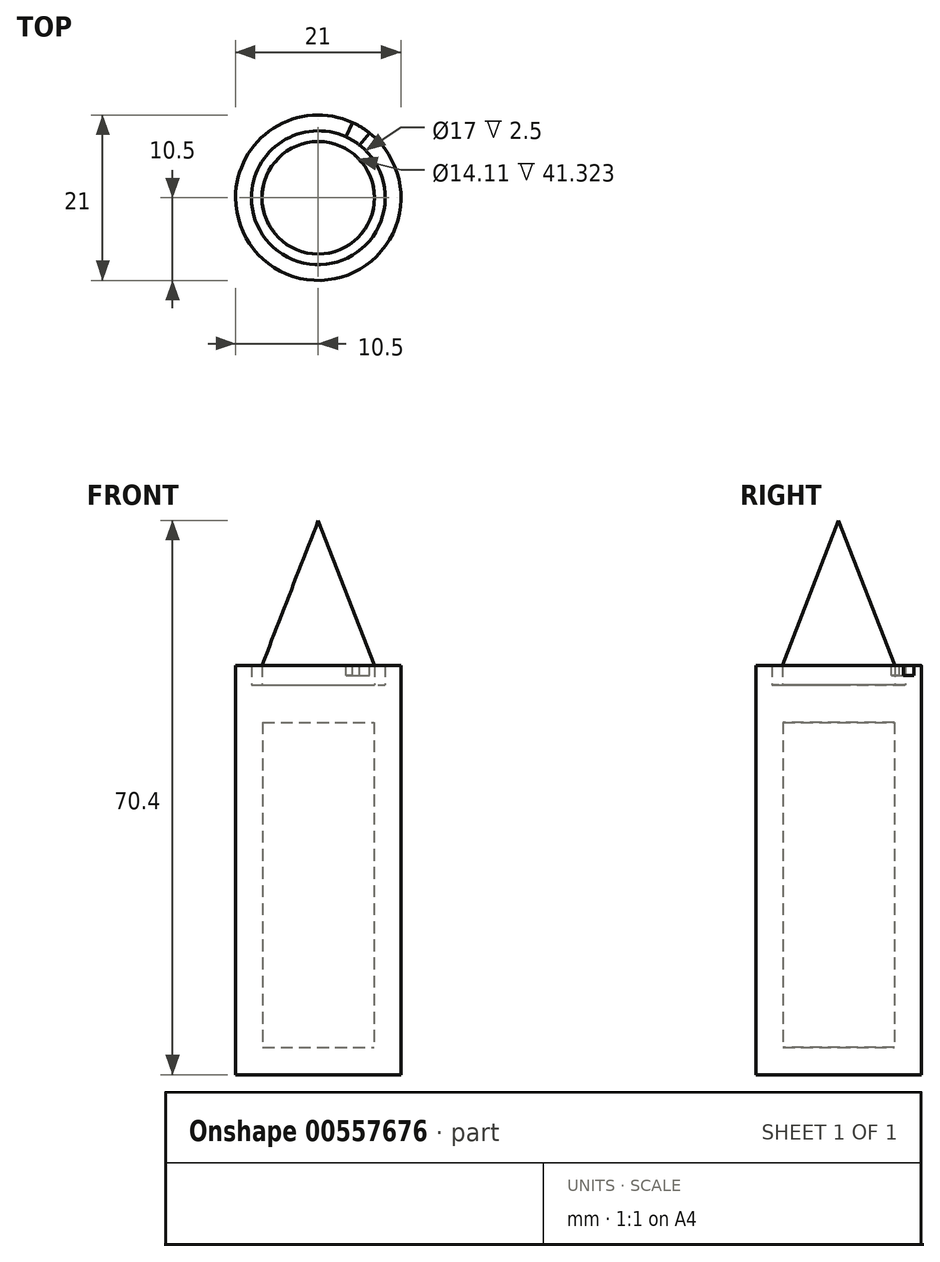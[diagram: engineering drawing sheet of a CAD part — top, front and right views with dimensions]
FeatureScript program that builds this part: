
annotation { "Feature Type Name" : "Feature", "Feature Type Description" : "" }
export const myFeature = defineFeature(function(context is Context, id is Id, definition is map)
    precondition{}
    {
        {
            var Q0;
            Q0=qCreatedBy(makeId("Front.planeOp"),FACE);
            var sketch = newSketch(context, id + "F0", { "sketchPlane" : qUnion([Q0])});
            skLineSegment(sketch, "E0", {"start": v(0, 0) * mm, "end": v(10.5, 0) * mm});
            skLineSegment(sketch, "E1", {"start": v(10.5, 0) * mm, "end": v(10.5, 52) * mm});
            skLineSegment(sketch, "E2", {"start": v(10.5, 52) * mm, "end": v(8.5, 52) * mm});
            skLineSegment(sketch, "E3", {"start": v(8.5, 52) * mm, "end": v(8.5, 49.5) * mm});
            skLineSegment(sketch, "E4", {"start": v(8.5, 49.5) * mm, "end": v(7.15, 49.5) * mm});
            skLineSegment(sketch, "E5", {"start": v(7.15, 49.5) * mm, "end": v(7.15, 52) * mm});
            skLineSegment(sketch, "E6", {"start": v(0, 0) * mm, "end": v(0, 70.4) * mm});
            skLineSegment(sketch, "E7", {"start": v(0, 70.4) * mm, "end": v(7.15, 52) * mm});
            skLineSegment(sketch, "E8.bottom", {"start": v(7.05, 3.45) * mm, "end": v(0, 3.45) * mm});
            skLineSegment(sketch, "E8.top", {"start": v(7.05, 44.77) * mm, "end": v(0, 44.77) * mm});
            skLineSegment(sketch, "E8.left", {"start": v(7.05, 3.45) * mm, "end": v(7.05, 44.77) * mm});
            skLineSegment(sketch, "E8.right", {"start": v(0, 3.45) * mm, "end": v(0, 44.77) * mm});
            skSolve(sketch);
        }
        {
            var Q0;
            {var subQ5=sQuery(id+"F0.wireOp",EDGE,"E0");Q0=makeQuery(id+"F0.imprint","IMPRINT",FACE,{"disambiguationData":[TD([[makeQuery(id+"F0.imprint","IMPRINT",EDGE,{"derivedFrom":subQ5}),1.0]])]});}
            var Q1;
            Q1=sQuery(id+"F0.wireOp",EDGE,"E6");
            revolve(context, id + "F1", {"entities" : qUnion([Q0]), "axis" : qUnion([Q1]), "revolveType" : RevolveType.FULL});
        }
        {
            var Q0;
            Q0=makeQuery(id+"F1.opRevolve","SWEPT_FACE",FACE,{"disambiguationData":[OSD([sQuery(id+"F0.wireOp",EDGE,"E2")])]});
            var sketch = newSketch(context, id + "F2", { "sketchPlane" : qUnion([Q0])});
            skLineSegment(sketch, "E9", {"start": v(4.36, 9.55) * mm, "end": v(3.5, 7.74) * mm});
            skLineSegment(sketch, "E10", {"start": v(5.24, 6.7) * mm, "end": v(6.52, 8.23) * mm});
            skSolve(sketch);
        }
        {
            var Q0;
            {var subQ0=sQuery(id+"F2.wireOp",EDGE,"E9");Q0=makeQuery(id+"F2.imprint","IMPRINT",FACE,{"disambiguationData":[TD([[makeQuery(id+"F2.imprint","IMPRINT",EDGE,{"derivedFrom":subQ0}),1.0]])]});}
            extrude(context, id + "F3", {"entities" : qUnion([Q0]), "operationType" : NewBodyOperationType.REMOVE, "oppositeDirection" : true, "depth" : 1.3 * mm, "offsetDistance" : 25 * mm});
        }
    });
